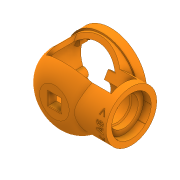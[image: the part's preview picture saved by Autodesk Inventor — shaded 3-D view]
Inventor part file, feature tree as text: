
AUTODESK INVENTOR PART (.ipt)
format: ipt  version: 2020 (Build 240168000, 168)  size: 923,648 bytes
history: native  units: in
note: dims shown in document units (in); Inventor stores cm internally (conversion verified against a paired STEP export)
features: sketch x27, extrude x24, plane x8, chamfer x6, projected_geometry x5, fillet x2, revolve x1, emboss x1
ambient origin geometry x8: Origin, YZ Plane, XZ Plane, XY Plane, X Axis, Y Axis, Z Axis, Center Point
bodies: Solid1 (feature_tree)
feature tree (74):
  extrude  "Extrusion1"  Depth=0.315in TaperAngle=0.0deg
  chamfer  "Chamfer1"  Distance=0.315in
  extrude  "Extrusion2"  Depth=2.3622in TaperAngle=360.0deg
  extrude  "Extrusion3"  Depth=0.0197in TaperAngle=0.0deg
  extrude  "Extrusion4"  Depth=0.1575in TaperAngle=0.0deg
  extrude  "Extrusion5"  Depth=1.2598in TaperAngle=0.0deg
  revolve  "Revolution1"  [1 undecoded]
  plane  "Work Plane1"
  extrude  "Extrusion6"  Depth=0.1575in
  plane  "Work Plane2"
  plane  "Work Plane3"
  extrude  "Extrusion8"  [1 undecoded]
  extrude  "Extrusion9"  Depth=0.1575in TaperAngle=0.0deg
  chamfer  "Chamfer3"  Distance=1.8898in
  extrude  "Extrusion10"  Depth=1.8898in
  plane  "Work Plane4"
  extrude  "Extrusion11"  Depth=0.315in TaperAngle=0.0deg
  extrude  "Extrusion12"  Depth=0.2756in
  extrude  "Extrusion13"  Depth=3.1496in TaperAngle=360.0deg
  plane  "Work Plane5"
  extrude  "Extrusion15"  [1 undecoded]
  extrude  "Extrusion16"  Depth=0.4764in
  plane  "Work Plane6"
  extrude  "Extrusion18"  Depth=0.0787in
  extrude  "Extrusion20"  Depth=0.9843in
  extrude  "Extrusion21"  TaperAngle=60.0deg  [1 undecoded]
  extrude  "Extrusion22"  TaperAngle=0.0deg  [1 undecoded]
  chamfer  "Chamfer34"  Distance=2.3622in
  chamfer  "Chamfer35"  Distance=0.1969in
  fillet  "Fillet1"  [1 undecoded]
  plane  "Work Plane7"
  emboss  "Emboss1"
  chamfer  "Chamfer36"  Distance=0.1969in
  sketch  "Sketch25"  dims[d178=0.315in]
  plane  "Work Plane8"
  extrude  "Extrusion23"  Depth=0.0984in TaperAngle=0.0deg
  extrude  "Extrusion24"  Depth=0.0984in TaperAngle=0.0deg
  extrude  "Extrusion25"  Depth=0.0197in
  extrude  "Extrusion26"  Depth=0.0197in
  extrude  "Extrusion27"  Depth=0.0197in
  fillet  "Fillet3"  Radius=0.0394in
  extrude  "Extrusion29"  Depth=0.0197in
  chamfer  "Chamfer37"  Distance=2.126in
  sketch  "Sketch1"  dims[d0=0.4724in d1=0.315in d2=0.0in d3=0.315in d4=0.125in d5=0.0137in]
  sketch  "Sketch2"  dims[d6=0.0157in d7=2.3622in d9=360.0deg]
  sketch  "Sketch3"  dims[d11=0.315in d12=0.0in d13=0.0197in d14=0.0in]
  projected_geometry  "Projected Loop1"
  sketch  "Sketch4"  dims[d15=2.5591in d16=0.1575in d17=0.0in]
  sketch  "Sketch5"  dims[d18=0.1575in d19=1.2598in d20=0.0in]
  sketch  "Sketch6"  dims[d21=1.1024in d22=0.5512in]
  sketch  "Sketch7"  dims[d23=0.8465in d24=0.1575in]
  sketch  "Sketch9"  dims[d25=90.0deg d26=-2.1063in]
  sketch  "Sketch10"  dims[d27=0.1575in d28=0.1575in d29=0.0in d33=-0.1575in d41=1.8898in]
  sketch  "Sketch11"  dims[d42=1.2795in d43=1.8898in]
  sketch  "Sketch12"  dims[d44=0.2165in d45=0.315in d46=0.0in]
  sketch  "Sketch13"  dims[d47=1.1811in d48=0.0in d49=0.2756in d50=0.125in d51=0.0137in]
  sketch  "Sketch14"  dims[d52=0.0157in d53=3.1496in d55=360.0deg]
  sketch  "Sketch16"  dims[d57=0.2756in d58=0.0in d59=-0.2756in]
  sketch  "Sketch17"  dims[d61=0.9843in d62=0.0in d63=0.4764in]
  sketch  "Sketch19"  dims[d64=0.315in d65=0.0in d66=0.0787in]
  projected_geometry  "Projected Loop2"
  projected_geometry  "Projected Loop3"
  sketch  "Sketch21"  dims[d73=0.315in d74=0.0in d166=0.9843in]
  sketch  "Sketch22"  dims[d171=-0.2756in d172=60.0deg]
  sketch  "Sketch23"  dims[d173=60.0deg d174=0.0in]
  projected_geometry  "Projected Loop4"
  sketch  "Sketch24"  dims[d175=0.0in d176=2.3622in d177=0.0in]
  sketch  "Sketch28"  dims[d179=0.2067in]
  sketch  "Sketch29"  dims[d180=0.0787in]
  sketch  "Sketch30"  dims[d181=45.0deg d182=0.1969in d183=0.0in d187=-0.4921in d188=0.1969in d189=0.0in]
  projected_geometry  "Projected Loop5"
  sketch  "Sketch31"  dims[d193=0.315in d194=0.0984in d195=0.0in]
  sketch  "Sketch32"  dims[d196=0.2362in d197=0.0984in d198=0.0in]
  sketch  "Sketch34"  dims[d199=0.0984in d200=0.0in d201=0.0591in d202=0.125in d203=0.0137in d204=0.0591in d205=0.125in d206=0.0137in d207=0.0197in d209=0.0394in d210=0.0in d211=0.0787in d212=0.125in d213=0.0137in d214=2.126in d215=-0.1575in d217=0.4921in d218=0.0in d220=4.7244in d221=0.1083in d222=0.1575in d223=360.0deg d224=0.1969in d225=0.1969in d226=0.1969in d227=0.1969in d228=0.1969in d229=0.1969in d230=0.1969in d231=0.1969in d232=0.1969in d233=0.1969in d234=0.0787in d235=0.0787in d236=0.0787in d237=0.0787in d238=0.0787in d239=0.0787in d240=0.0787in d241=0.0787in d242=0.0787in d243=0.0787in d244=0.315in d245=0.0in d246=0.315in d247=0.0in d248=0.0591in d249=0.315in d250=0.0in d251=0.0394in d252=0.0in d253=0.4803in d254=0.4803in d257=0.0197in d258=0.0394in d259=0.2362in d260=0.0in d261=0.0394in d262=0.125in d263=45.0deg d264=0.0344in d265=0.0344in d266=0.5in d267=0.0344in]
note: 6 required parameter values undecoded (feature->parameter linkage not recoverable at this tier; creation-order binding heuristic only, values carry confidence <= 0.55)